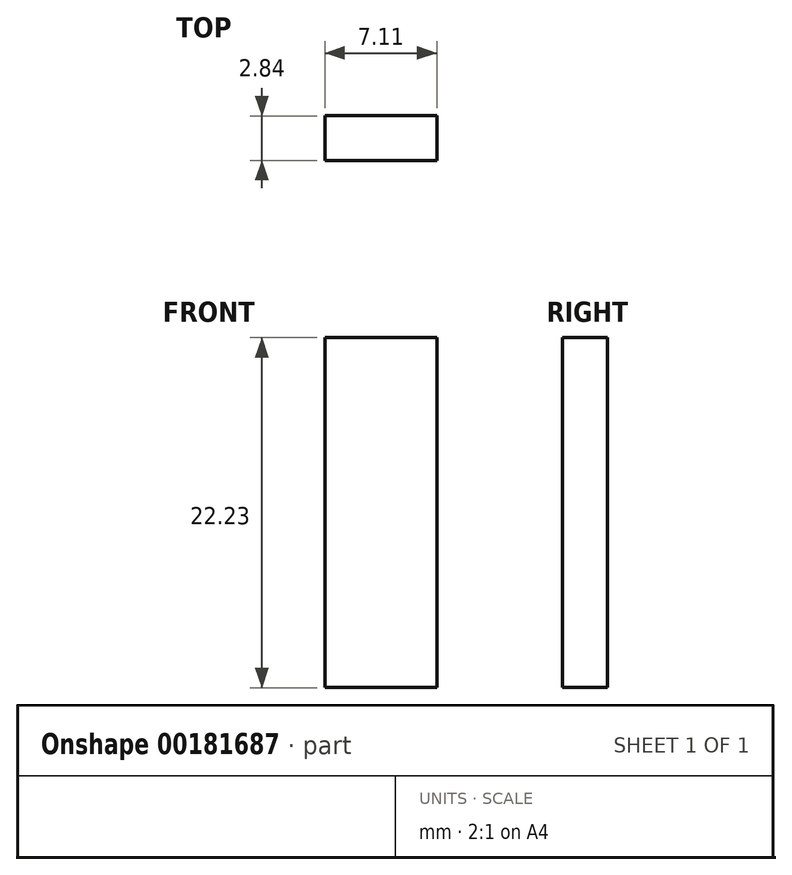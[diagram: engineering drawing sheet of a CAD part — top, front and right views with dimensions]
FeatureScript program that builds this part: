
annotation { "Feature Type Name" : "Feature", "Feature Type Description" : "" }
export const myFeature = defineFeature(function(context is Context, id is Id, definition is map)
    precondition{}
    {
        {
            var Q0;
            Q0=qCreatedBy(makeId("Top.planeOp"),FACE);
            var sketch = newSketch(context, id + "F0", { "sketchPlane" : qUnion([Q0])});
            skLineSegment(sketch, "E0.bottom", {"start": v(0, 0) * mm, "end": v(-7.11, 0) * mm});
            skLineSegment(sketch, "E0.top", {"start": v(0, 2.84) * mm, "end": v(-7.11, 2.84) * mm});
            skLineSegment(sketch, "E0.left", {"start": v(0, 0) * mm, "end": v(0, 2.84) * mm});
            skLineSegment(sketch, "E0.right", {"start": v(-7.11, 0) * mm, "end": v(-7.11, 2.84) * mm});
            skSolve(sketch);
        }
        {
            var Q0;
            Q0 = qSketchRegion(id + "F0", true);
            extrude(context, id + "F1", {"entities" : qUnion([Q0]), "oppositeDirection" : true, "depth" : 22.22 * mm});
        }
    });
